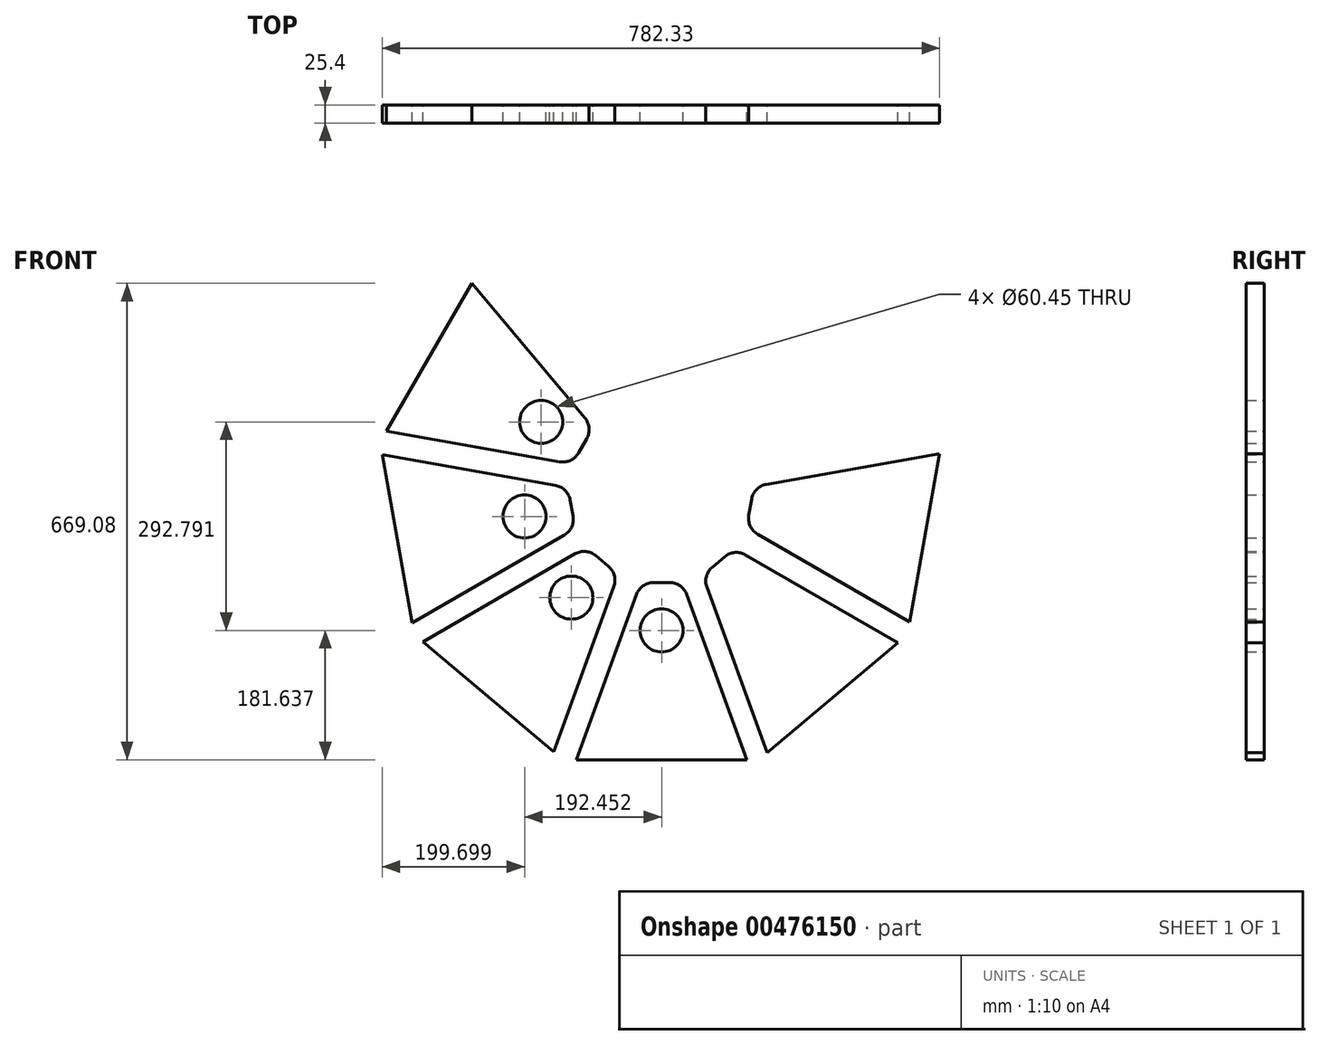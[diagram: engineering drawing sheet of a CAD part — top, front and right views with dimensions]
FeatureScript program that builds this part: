
annotation { "Feature Type Name" : "Feature", "Feature Type Description" : "" }
export const myFeature = defineFeature(function(context is Context, id is Id, definition is map)
    precondition{}
    {
        {
            var Q0;
            Q0=qCreatedBy(makeId("Front.planeOp"),FACE);
            var sketch = newSketch(context, id + "F0", { "sketchPlane" : qUnion([Q0])});
            skPoint(sketch, "E0.newPointA", {"position": v(-66.2, 128.1) * mm});
            skLineSegment(sketch, "E1", {"start": v(-91.4, 108.17) * mm, "end": v(-183.75, -145.59) * mm, "construction": true});
            skLineSegment(sketch, "E2.MirrorCS", {"start": v(-380.06, 23.2) * mm, "end": v(-166.2, 146.68) * mm});
            skLineSegment(sketch, "E3.MirrorCS", {"start": v(-288.21, -53.87) * mm, "end": v(-380.06, 23.2) * mm});
            skPoint(sketch, "E4.MirrorP", {"position": v(-130.7, 167.18) * mm});
            skLineSegment(sketch, "E5.MirrorCS", {"start": v(-288.21, -53.87) * mm, "end": v(-196.36, -130.94) * mm});
            skCircle(sketch, "E6.MirrorC", {"center": v(-171.46, 85.28) * mm, "radius": 30.23 * mm});
            skLineSegment(sketch, "E7.MirrorCS", {"start": v(-196.36, -130.94) * mm, "end": v(-111.9, 101.11) * mm});
            skLineSegment(sketch, "E8.MirrorCS", {"start": v(-119.45, 129.26) * mm, "end": v(-137.18, 144.14) * mm});
            skArc(sketch, "E9.MirrorCS", {"start": v(-166.2, 146.68) * mm, "mid": v(-151.29, 149.98) * mm, "end": v(-137.18, 144.14) * mm});
            skArc(sketch, "E10.MirrorCS", {"start": v(-119.45, 129.26) * mm, "mid": v(-111.24, 116.37) * mm, "end": v(-111.9, 101.11) * mm});
            skLineSegment(sketch, "E11", {"start": v(0, 107.62) * mm, "end": v(92.27, -145.9) * mm, "construction": true});
            skLineSegment(sketch, "E12.MirrorCS", {"start": v(77.6, 200.97) * mm, "end": v(81.61, 223.77) * mm});
            skLineSegment(sketch, "E13.MirrorCS", {"start": v(44.02, 142.83) * mm, "end": v(26.29, 127.95) * mm});
            skArc(sketch, "E14.MirrorCS", {"start": v(102.21, 244.37) * mm, "mid": v(88.66, 237.32) * mm, "end": v(81.61, 223.77) * mm});
            skPoint(sketch, "E15.MirrorP", {"position": v(61.84, 237.25) * mm});
            skPoint(sketch, "E16.MirrorP", {"position": v(37.54, 165.87) * mm});
            skArc(sketch, "E17.MirrorCS", {"start": v(77.6, 200.97) * mm, "mid": v(79.59, 185.83) * mm, "end": v(89.9, 174.57) * mm});
            skPoint(sketch, "E18.MirrorP", {"position": v(54.4, 195.07) * mm});
            skLineSegment(sketch, "E19.MirrorCS", {"start": v(303.76, 51.1) * mm, "end": v(89.9, 174.57) * mm});
            skLineSegment(sketch, "E20.MirrorCS", {"start": v(13.63, 161.04) * mm, "end": v(195.06, -55.18) * mm, "construction": true});
            skLineSegment(sketch, "E21.MirrorCS", {"start": v(195.06, -55.18) * mm, "end": v(286.9, 21.9) * mm});
            skLineSegment(sketch, "E22.MirrorCS", {"start": v(195.06, -55.18) * mm, "end": v(103.2, -132.25) * mm});
            skArc(sketch, "E23.MirrorCS", {"start": v(44.02, 142.83) * mm, "mid": v(58.13, 148.67) * mm, "end": v(73.05, 145.37) * mm});
            skLineSegment(sketch, "E24.MirrorCS", {"start": v(286.9, 21.9) * mm, "end": v(73.05, 145.37) * mm});
            skArc(sketch, "E25.MirrorCS", {"start": v(18.75, 99.8) * mm, "mid": v(18.08, 115.06) * mm, "end": v(26.29, 127.95) * mm});
            skLineSegment(sketch, "E26.MirrorCS", {"start": v(103.2, -132.25) * mm, "end": v(18.75, 99.8) * mm});
            skLineSegment(sketch, "E27.MirrorCS", {"start": v(69.66, 166.79) * mm, "end": v(303.52, 31.77) * mm, "construction": true});
            skLineSegment(sketch, "E28.MirrorCS", {"start": v(324.58, 169.17) * mm, "end": v(345.4, 287.25) * mm});
            skLineSegment(sketch, "E29.MirrorCS", {"start": v(324.58, 169.17) * mm, "end": v(303.76, 51.1) * mm});
            skLineSegment(sketch, "E30.MirrorCS", {"start": v(345.4, 287.25) * mm, "end": v(102.21, 244.37) * mm});
            skLineSegment(sketch, "E31", {"start": v(-169.96, 162.09) * mm, "end": v(-387.51, 36.48) * mm, "construction": true});
            skLineSegment(sketch, "E32.MirrorCS", {"start": v(-177.37, 257.08) * mm, "end": v(-443.3, 303.98) * mm, "construction": true});
            skLineSegment(sketch, "E33.MirrorCS", {"start": v(-436.93, 285.73) * mm, "end": v(-193.74, 242.85) * mm});
            skLineSegment(sketch, "E34.MirrorCS", {"start": v(-416.1, 167.65) * mm, "end": v(-436.93, 285.73) * mm});
            skLineSegment(sketch, "E35.MirrorCS", {"start": v(-416.1, 167.65) * mm, "end": v(-395.29, 49.58) * mm});
            skLineSegment(sketch, "E36.MirrorCS", {"start": v(-395.29, 49.58) * mm, "end": v(-181.43, 173.05) * mm});
            skArc(sketch, "E37.MirrorCS", {"start": v(-181.43, 173.05) * mm, "mid": v(-171.1, 184.3) * mm, "end": v(-169.11, 199.45) * mm});
            skLineSegment(sketch, "E38.MirrorCS", {"start": v(-173.13, 222.25) * mm, "end": v(-169.11, 199.45) * mm});
            skArc(sketch, "E39.MirrorCS", {"start": v(-173.13, 222.25) * mm, "mid": v(-180.19, 235.8) * mm, "end": v(-193.74, 242.85) * mm});
            skCircle(sketch, "E40.MirrorC", {"center": v(-237.23, 199.2) * mm, "radius": 30.23 * mm});
            skLineSegment(sketch, "E41.MirrorCS", {"start": v(-164.68, -142.47) * mm, "end": v(-80.22, 89.58) * mm});
            skLineSegment(sketch, "E42.MirrorCS", {"start": v(75.12, -142.47) * mm, "end": v(-9.34, 89.58) * mm});
            skCircle(sketch, "E43.MirrorC", {"center": v(-44.78, 39.17) * mm, "radius": 30.23 * mm});
            skLineSegment(sketch, "E44.MirrorCS", {"start": v(-56.35, 106.3) * mm, "end": v(-33.2, 106.3) * mm});
            skArc(sketch, "E45.MirrorCS", {"start": v(-56.35, 106.3) * mm, "mid": v(-70.92, 101.7) * mm, "end": v(-80.22, 89.58) * mm});
            skArc(sketch, "E46.MirrorCS", {"start": v(-9.34, 89.58) * mm, "mid": v(-18.64, 101.7) * mm, "end": v(-33.2, 106.3) * mm});
            skLineSegment(sketch, "E47.MirrorCS", {"start": v(-44.78, -142.47) * mm, "end": v(-164.68, -142.47) * mm});
            skLineSegment(sketch, "E48.MirrorCS", {"start": v(-44.78, -142.47) * mm, "end": v(75.12, -142.47) * mm});
            skLineSegment(sketch, "E49.MirrorCS", {"start": v(-431.07, 318.94) * mm, "end": v(-187.88, 276.06) * mm});
            skCircle(sketch, "E50.MirrorC", {"center": v(-213.82, 331.96) * mm, "radius": 30.23 * mm});
            skLineSegment(sketch, "E51.MirrorCS", {"start": v(-311.17, 526.61) * mm, "end": v(-152.44, 337.44) * mm});
            skArc(sketch, "E52.MirrorCS", {"start": v(-152.44, 337.44) * mm, "mid": v(-146.6, 323.33) * mm, "end": v(-149.9, 308.42) * mm});
            skLineSegment(sketch, "E53.MirrorCS", {"start": v(-161.47, 288.37) * mm, "end": v(-149.9, 308.42) * mm});
            skArc(sketch, "E54.MirrorCS", {"start": v(-161.47, 288.37) * mm, "mid": v(-172.74, 278.05) * mm, "end": v(-187.88, 276.06) * mm});
            skLineSegment(sketch, "E55.MirrorCS", {"start": v(-371.12, 422.77) * mm, "end": v(-431.07, 318.94) * mm});
            skLineSegment(sketch, "E56.MirrorCS", {"start": v(-371.12, 422.77) * mm, "end": v(-311.17, 526.61) * mm});
            skSolve(sketch);
        }
        {
            var Q0;
            Q0=qSketchRegion(id+"F0",true);
            extrude(context, id + "F1", {"entities" : qUnion([Q0]), "depth" : 25.4 * mm});
        }
    });
